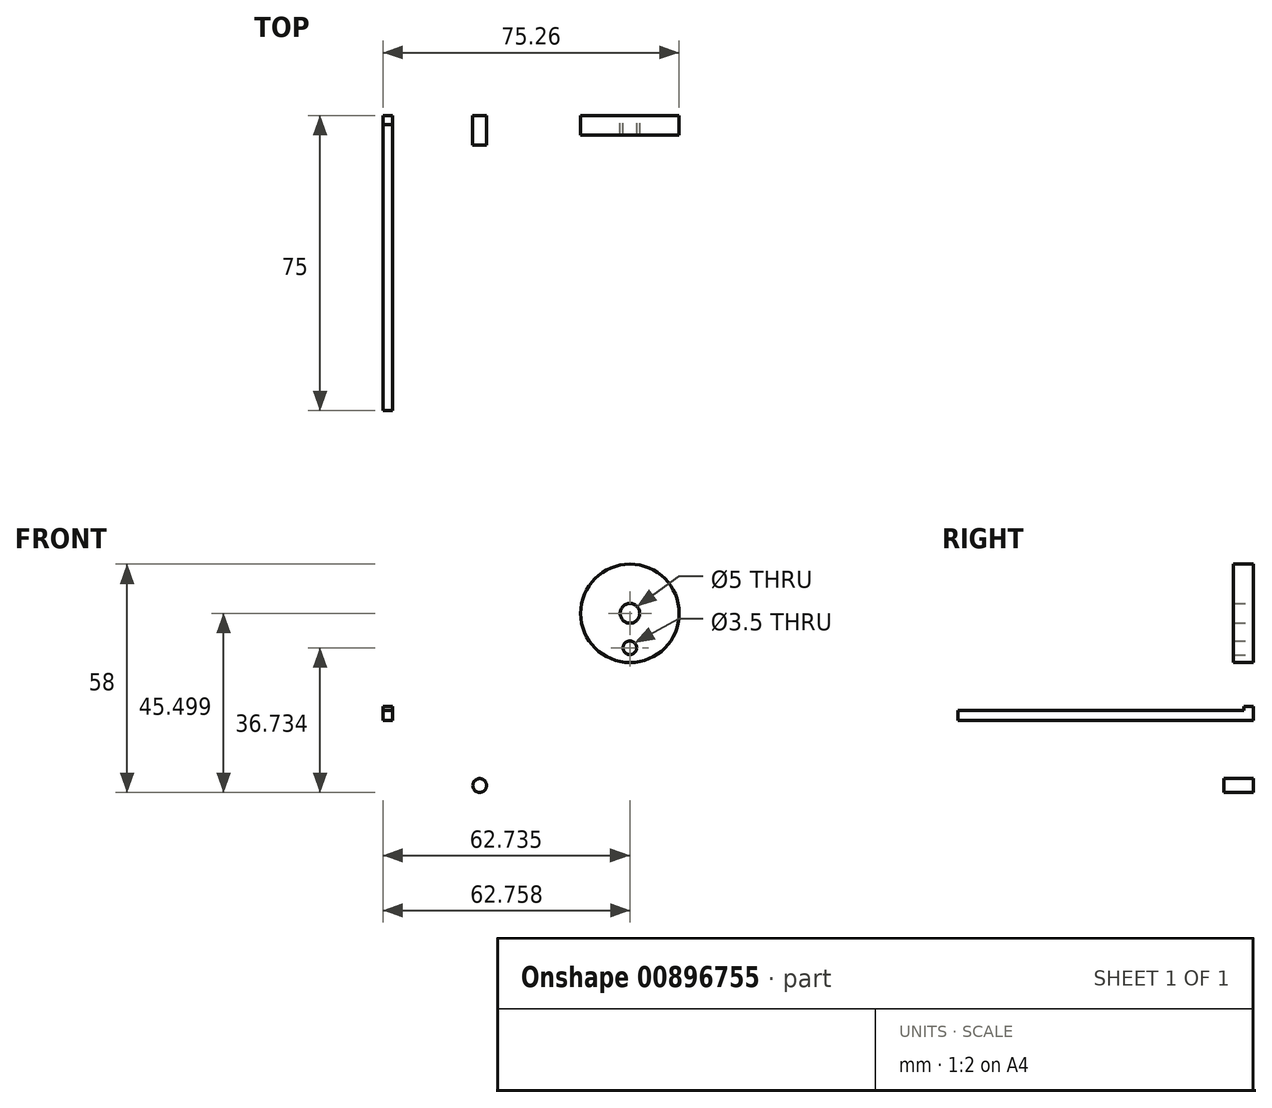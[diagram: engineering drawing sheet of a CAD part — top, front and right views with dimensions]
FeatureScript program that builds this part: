
annotation { "Feature Type Name" : "Feature", "Feature Type Description" : "" }
export const myFeature = defineFeature(function(context is Context, id is Id, definition is map)
    precondition{}
    {
        {
            var Q0;
            Q0=qCreatedBy(makeId("Front.planeOp"),FACE);
            var sketch = newSketch(context, id + "F0", { "sketchPlane" : qUnion([Q0])});
            skCircle(sketch, "E0", {"center": v(23.13, 24.1) * mm, "radius": 12.5 * mm});
            skSolve(sketch);
        }
        {
            var Q0;
            Q0=makeQuery(id+"F0.imprint","IMPRINT",FACE,{"disambiguationData":[TD([[makeQuery(id+"F0.imprint","IMPRINT",EDGE,{"derivedFrom":sQuery(id+"F0.wireOp",EDGE,"E0")}),1.0]])]});
            extrude(context, id + "F1", {"entities" : qUnion([Q0]), "depth" : 5 * mm, "offsetDistance" : 25 * mm});
        }
        {
            var Q0;
            Q0=sQuery(id+"F0.wireOp",VERTEX,"E0.center");
            var Q1;
            Q1=makeQuery(id+"F1.opExtrude","SWEPT_BODY",BODY,{"disambiguationData":[OSD([sQuery(id+"F0.wireOp",EDGE,"E0")])]});
            hole(context, id + "F2", {"style" : HoleStyle.SIMPLE, "endStyle" : HoleEndStyle.BLIND, "oppositeDirection" : true, "holeDiameter" : 5 * mm, "majorDiameter" : 5 * mm, "holeDepth" : 5 * mm, "isTappedThrough" : true, "tappedDepth" : 12 * mm, "tapClearance" : 3, "locations" : qUnion([Q0]), "scope" : qUnion([Q1])});
        }
        {
            var Q0;
            Q0=makeQuery(id+"F0.imprint","IMPRINT",FACE,{"disambiguationData":[TD([[makeQuery(id+"F0.imprint","IMPRINT",EDGE,{"derivedFrom":sQuery(id+"F0.wireOp",EDGE,"E0")}),1.0]])]});
            var sketch = newSketch(context, id + "F3", { "sketchPlane" : qUnion([Q0])});
            skLineSegment(sketch, "E1", {"start": v(23.1, 24.09) * mm, "end": v(23.1, 11.52) * mm});
            skLineSegment(sketch, "E2", {"start": v(23.1, 11.52) * mm, "end": v(23.1, 15.33) * mm});
            skLineSegment(sketch, "E3.bottom", {"start": v(21.85, 14.08) * mm, "end": v(24.35, 14.08) * mm});
            skLineSegment(sketch, "E3.top", {"start": v(21.85, 16.58) * mm, "end": v(24.35, 16.58) * mm});
            skLineSegment(sketch, "E3.left", {"start": v(21.85, 14.08) * mm, "end": v(21.85, 16.58) * mm});
            skLineSegment(sketch, "E3.right", {"start": v(24.35, 14.08) * mm, "end": v(24.35, 16.58) * mm});
            skPoint(sketch, "E3.middle", {"position": v(23.1, 15.33) * mm});
            skSolve(sketch);
        }
        {
            var Q0;
            Q0=sQuery(id+"F3.wireOp",VERTEX,"E3.middle");
            var Q1;
            Q1=makeQuery(id+"F1.opExtrude","SWEPT_BODY",BODY,{"disambiguationData":[OSD([sQuery(id+"F0.wireOp",EDGE,"E0")])]});
            hole(context, id + "F4", {"style" : HoleStyle.SIMPLE, "endStyle" : HoleEndStyle.BLIND, "oppositeDirection" : true, "holeDiameter" : 3.5 * mm, "majorDiameter" : 5 * mm, "holeDepth" : 5 * mm, "isTappedThrough" : true, "tappedDepth" : 12 * mm, "tapClearance" : 3, "locations" : qUnion([Q0]), "scope" : qUnion([Q1])});
        }
        {
            var Q0;
            Q0=qCreatedBy(makeId("Front.planeOp"),FACE);
            var sketch = newSketch(context, id + "F5", { "sketchPlane" : qUnion([Q0])});
            skCircle(sketch, "E4", {"center": v(-15.06, -19.65) * mm, "radius": 1.75 * mm});
            skSolve(sketch);
        }
        {
            var Q0;
            Q0=makeQuery(id+"F5.imprint","IMPRINT",FACE,{"disambiguationData":[TD([[makeQuery(id+"F5.imprint","IMPRINT",EDGE,{"derivedFrom":sQuery(id+"F5.wireOp",EDGE,"E4")}),1.0]])]});
            extrude(context, id + "F6", {"entities" : qUnion([Q0]), "depth" : 7.5 * mm, "offsetDistance" : 25 * mm});
        }
        {
            var Q0;
            Q0=qCreatedBy(makeId("Front.planeOp"),FACE);
            var sketch = newSketch(context, id + "F7", { "sketchPlane" : qUnion([Q0])});
            skLineSegment(sketch, "E5.bottom", {"start": v(-39.63, -3.1) * mm, "end": v(-37.13, -3.1) * mm});
            skLineSegment(sketch, "E5.top", {"start": v(-39.63, -0.6) * mm, "end": v(-37.13, -0.6) * mm});
            skLineSegment(sketch, "E5.left", {"start": v(-39.63, -3.1) * mm, "end": v(-39.63, -0.6) * mm});
            skLineSegment(sketch, "E5.right", {"start": v(-37.13, -3.1) * mm, "end": v(-37.13, -0.6) * mm});
            skSolve(sketch);
        }
        {
            var Q0;
            Q0=makeQuery(id+"F7.imprint","IMPRINT",FACE,{"disambiguationData":[TD([[makeQuery(id+"F7.imprint","IMPRINT",EDGE,{"derivedFrom":sQuery(id+"F7.wireOp",EDGE,"E5.bottom")}),1.0]])]});
            extrude(context, id + "F8", {"entities" : qUnion([Q0]), "depth" : 75 * mm, "offsetDistance" : 25 * mm});
        }
        {
            var Q0;
            Q0=makeQuery(id+"F8.opExtrude","SWEPT_FACE",FACE,{"disambiguationData":[OSD([sQuery(id+"F7.wireOp",EDGE,"E5.top")])]});
            var sketch = newSketch(context, id + "F9", { "sketchPlane" : qUnion([Q0])});
            skLineSegment(sketch, "E6.bottom", {"start": v(-39.63, 0) * mm, "end": v(-37.13, 0) * mm});
            skLineSegment(sketch, "E6.top", {"start": v(-39.63, -2.32) * mm, "end": v(-37.13, -2.32) * mm});
            skLineSegment(sketch, "E6.left", {"start": v(-39.63, 0) * mm, "end": v(-39.63, -2.32) * mm});
            skLineSegment(sketch, "E6.right", {"start": v(-37.13, 0) * mm, "end": v(-37.13, -2.32) * mm});
            skSolve(sketch);
        }
        {
            var Q0;
            Q0=makeQuery(id+"F9.imprint","IMPRINT",FACE,{"disambiguationData":[TD([[makeQuery(id+"F9.imprint","IMPRINT",EDGE,{"derivedFrom":sQuery(id+"F9.wireOp",EDGE,"E6.bottom")}),-1.0]])]});
            extrude(context, id + "F10", {"entities" : qUnion([Q0]), "operationType" : NewBodyOperationType.ADD, "depth" : 1 * mm, "offsetDistance" : 25 * mm});
        }
    });
